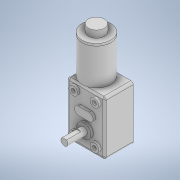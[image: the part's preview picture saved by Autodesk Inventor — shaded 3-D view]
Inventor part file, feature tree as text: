
AUTODESK INVENTOR PART (.ipt)
format: ipt  version: 2020 (Build 240168000, 168)  size: 246,784 bytes
history: native  units: mm
features: sketch x8, extrude x7, projected_geometry x7, chamfer x2, hole x1, fillet x1
ambient origin geometry x8: Origin, YZ Plane, XZ Plane, XY Plane, X Axis, Y Axis, Z Axis, Center Point
bodies: Solid1 (feature_tree), Solid2 (feature_tree)
feature tree (26):
  extrude  "Extrusion1"  Depth=25.0mm
  extrude  "Extrusion3"  Depth=46.0mm
  extrude  "Extrusion4"  Depth=30.8mm
  extrude  "Extrusion5"  Depth=32.0mm
  hole  "Hole1"  [1 undecoded]
  fillet  "Fillet1"  Radius=12.0mm
  chamfer  "Chamfer9"  Distance=15.0mm
  chamfer  "Chamfer10"  Distance=7.0mm
  extrude  "Extrusion2"  Depth=7.0mm
  extrude  "Extrusion6"  Depth=2.0mm TaperAngle=0.0deg
  extrude  "Extrusion7"  Depth=6.0mm
  sketch  "Sketch1"  dims[d0=32.0mm d1=25.0mm]
  sketch  "Sketch2"  dims[d2=46.0mm d3=0.0mm d4=24.4mm]
  projected_geometry  "Projected Loop1"
  sketch  "Sketch3"  dims[d5=30.8mm d6=0.0mm d7=7.4mm]
  projected_geometry  "Projected Loop2"
  sketch  "Sketch4"  dims[d8=6.0mm d9=32.0mm]
  projected_geometry  "Projected Loop3"
  sketch  "Sketch5"  dims[d11=20.0mm d13=18.0mm d14=20.0mm d16=33.0mm d19=3.3mm d20=12.0mm]
  projected_geometry  "Projected Loop4"
  sketch  "Sketch6"  dims[d21=15.0mm]
  projected_geometry  "Projected Loop5"
  sketch  "Sketch7"  dims[d22=16.0mm]
  projected_geometry  "Projected Loop6"
  sketch  "Sketch8"  dims[d23=7.0mm d24=15.0mm d25=7.0mm d26=7.0mm d27=2.0mm d28=0.0mm d29=6.0mm d30=16.5mm d31=0.0mm d33=12.0mm d34=0.0mm d35=5.4mm d36=20.0mm d38=18.0mm d39=20.0mm d41=33.0mm d44=3.4mm d45=6.0mm d46=11.0mm d47=2.6mm d48=90.0deg d49=4.0mm d50=20.594885mm d51=2.0mm d52=0.0mm d53=13.5mm d54=6.0mm d55=0.0mm d80=2.0mm d81=1.0mm d82=2.0mm d83=45.0deg d84=1.0mm d85=2.0mm d86=45.0deg]
  projected_geometry  "Projected Loop7"
note: 1 required parameter value undecoded (feature->parameter linkage not recoverable at this tier; creation-order binding heuristic only, values carry confidence <= 0.55)
